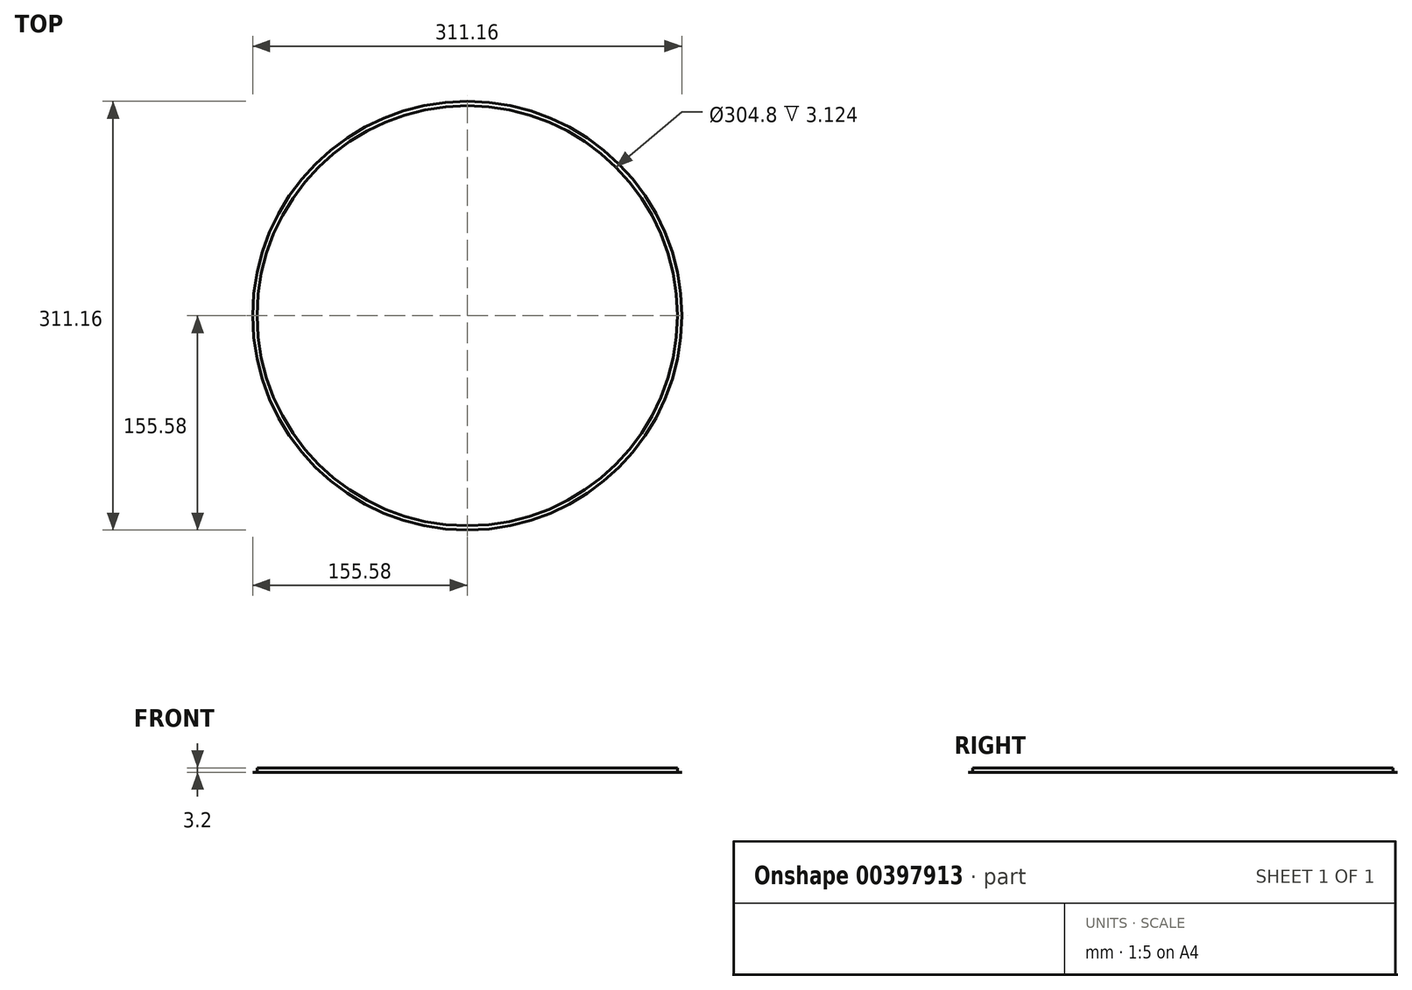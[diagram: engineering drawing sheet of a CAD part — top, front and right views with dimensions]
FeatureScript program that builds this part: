
annotation { "Feature Type Name" : "Feature", "Feature Type Description" : "" }
export const myFeature = defineFeature(function(context is Context, id is Id, definition is map)
    precondition{}
    {
        {
            var Q0;
            Q0=qCreatedBy(makeId("Top.planeOp"),FACE);
            var sketch = newSketch(context, id + "F0", { "sketchPlane" : qUnion([Q0])});
            skCircle(sketch, "E0", {"center": v(0, 0) * mm, "radius": 152.4 * mm});
            skCircle(sketch, "E1", {"center": v(0, 0) * mm, "radius": 152.44 * mm});
            skCircle(sketch, "E2", {"center": v(0, 0) * mm, "radius": 155.58 * mm});
            skSolve(sketch);
        }
        {
            var Q0;
            Q0=makeQuery(id+"F0.imprint","IMPRINT",FACE,{"disambiguationData":[TD([[makeQuery(id+"F0.imprint","IMPRINT",EDGE,{"derivedFrom":sQuery(id+"F0.wireOp",EDGE,"E0")}),1.0]])]});
            extrude(context, id + "F1", {"entities" : qUnion([Q0]), "oppositeDirection" : true, "depth" : 0.08 * mm});
        }
        {
            var Q0;
            Q0=makeQuery(id+"F0.imprint","IMPRINT",FACE,{"disambiguationData":[TD([[makeQuery(id+"F0.imprint","IMPRINT",EDGE,{"derivedFrom":sQuery(id+"F0.wireOp",EDGE,"E0")}),-1.0]])]});
            var Q1;
            Q1=makeQuery(id+"F0.imprint","IMPRINT",FACE,{"disambiguationData":[TD([[makeQuery(id+"F0.imprint","IMPRINT",EDGE,{"derivedFrom":sQuery(id+"F0.wireOp",EDGE,"E1")}),-1.0]])]});
            extrude(context, id + "F2", {"entities" : qUnion([Q0, Q1]), "operationType" : NewBodyOperationType.ADD, "oppositeDirection" : true, "depth" : 3.2 * mm});
        }
        {
            var Q0;
            Q0=makeQuery(id+"F0.imprint","IMPRINT",FACE,{"disambiguationData":[TD([[makeQuery(id+"F0.imprint","IMPRINT",EDGE,{"derivedFrom":sQuery(id+"F0.wireOp",EDGE,"E1")}),-1.0]])]});
            extrude(context, id + "F3", {"entities" : qUnion([Q0]), "operationType" : NewBodyOperationType.REMOVE, "oppositeDirection" : true, "depth" : 3.17 * mm});
        }
    });
